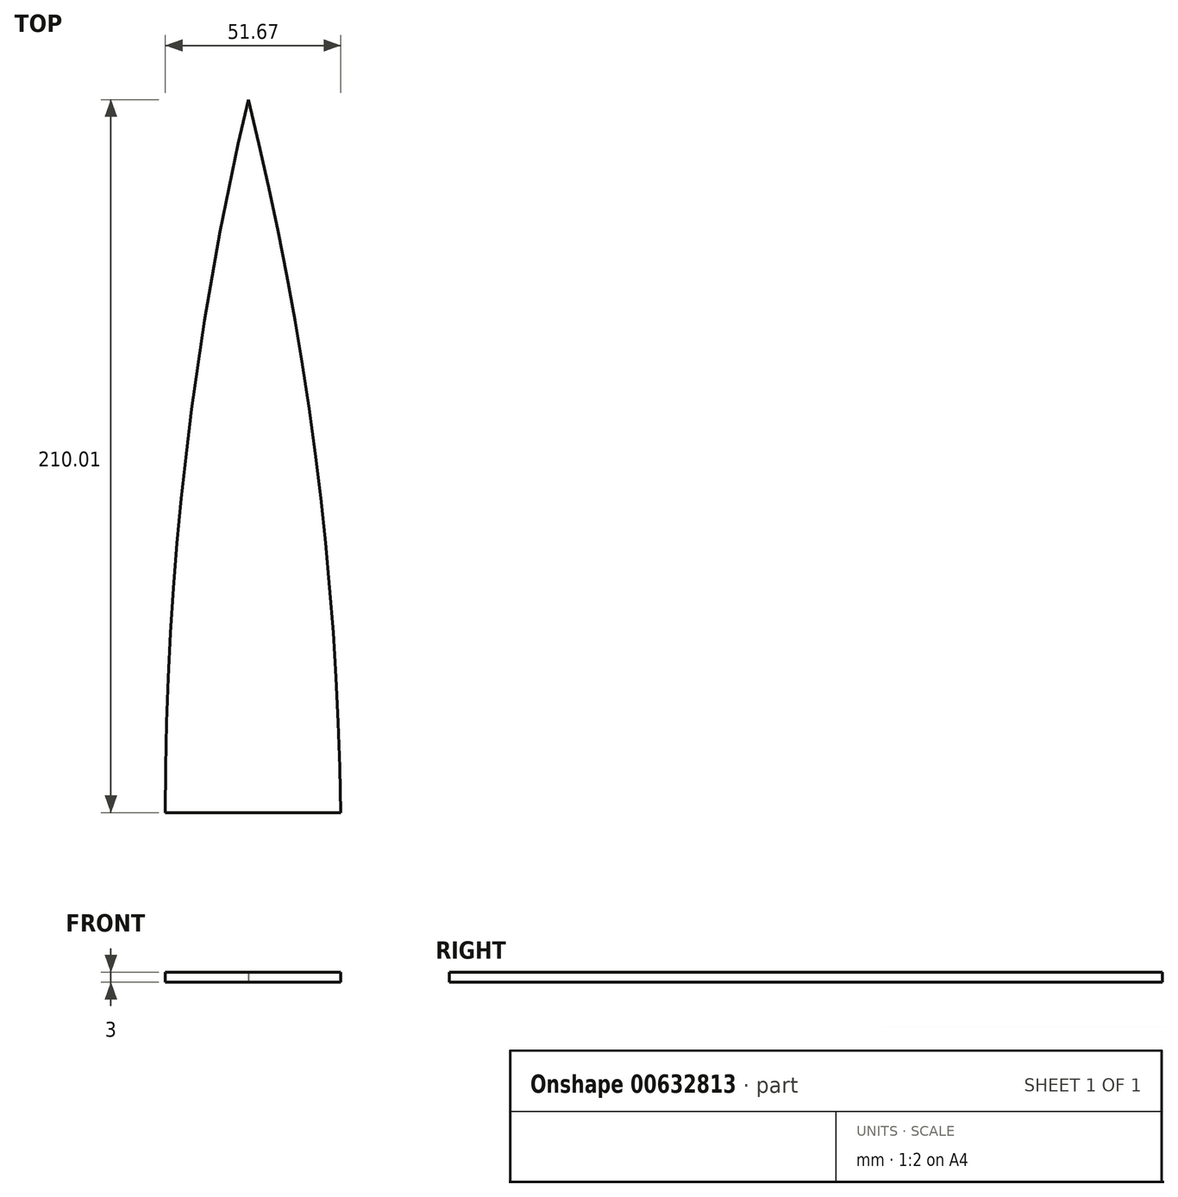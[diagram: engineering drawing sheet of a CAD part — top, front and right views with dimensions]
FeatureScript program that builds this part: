
annotation { "Feature Type Name" : "Feature", "Feature Type Description" : "" }
export const myFeature = defineFeature(function(context is Context, id is Id, definition is map)
    precondition{}
    {
        {
            var Q0;
            Q0=qCreatedBy(makeId("Top.planeOp"),FACE);
            var sketch = newSketch(context, id + "F0", { "sketchPlane" : qUnion([Q0])});
            skLineSegment(sketch, "E0.bottom", {"start": v(0, 0) * mm, "end": v(-51.67, 0) * mm, "construction": true});
            skArc(sketch, "E1", {"start": v(-51.67, 0) * mm, "mid": v(-45.54, 105.71) * mm, "end": v(-27.22, 210.01) * mm});
            skArc(sketch, "E2.MirrorCS", {"start": v(0, 0) * mm, "mid": v(-7.51, 105.8) * mm, "end": v(-27.22, 210.01) * mm});
            skLineSegment(sketch, "E3", {"start": v(-51.67, 0) * mm, "end": v(0, 0) * mm});
            skLineSegment(sketch, "E4", {"start": v(-27.22, 210.01) * mm, "end": v(-27.22, 0) * mm, "construction": true});
            skSolve(sketch);
        }
        {
            var Q0;
            Q0 = qSketchRegion(id + "F0", true);
            extrude(context, id + "F1", {"entities" : qUnion([Q0]), "depth" : 3 * mm, "offsetDistance" : 25 * mm});
        }
    });
